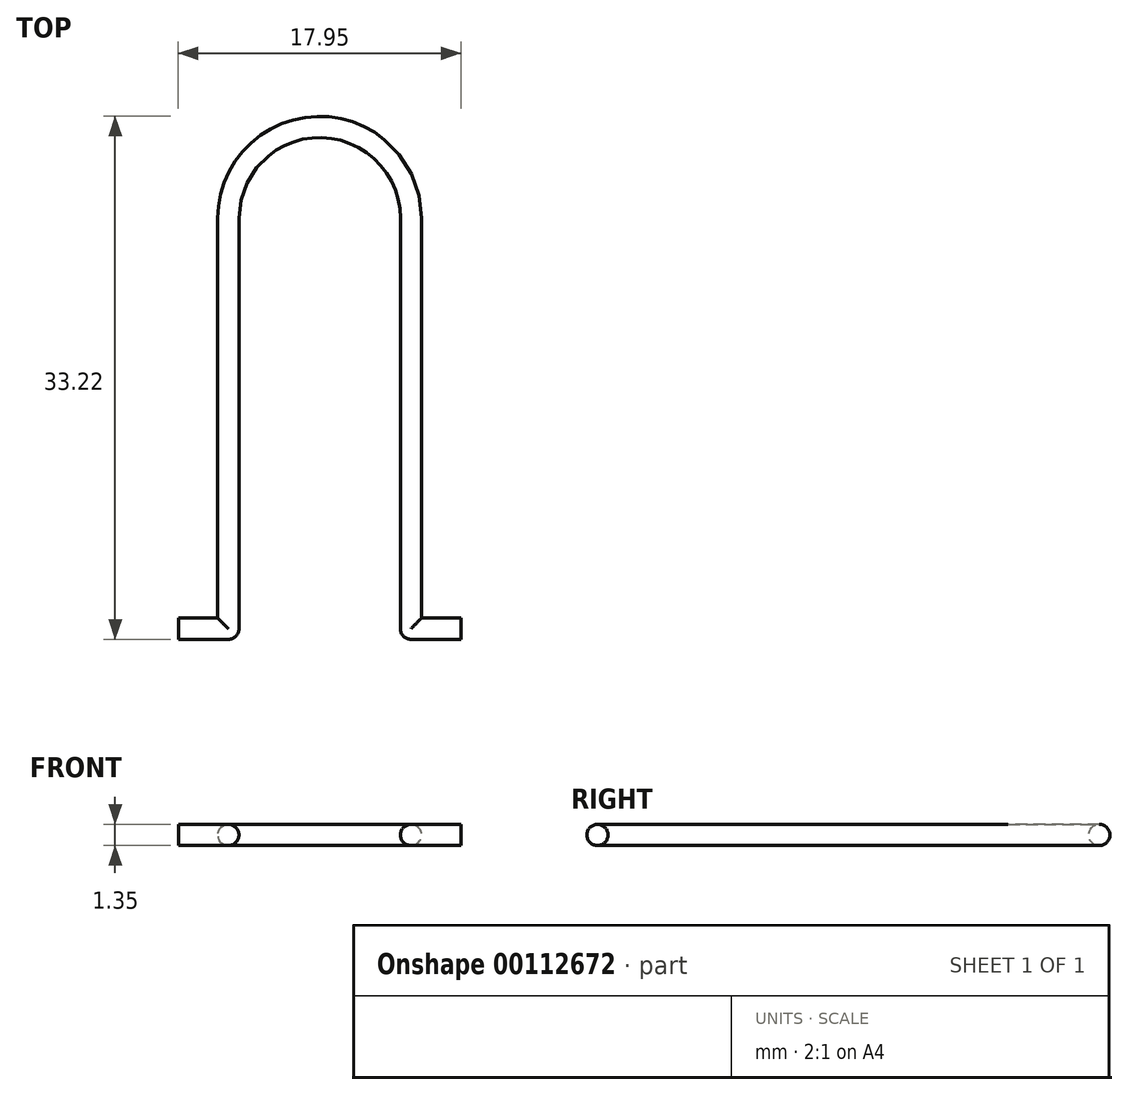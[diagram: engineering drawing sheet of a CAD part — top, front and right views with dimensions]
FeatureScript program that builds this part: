
annotation { "Feature Type Name" : "Feature", "Feature Type Description" : "" }
export const myFeature = defineFeature(function(context is Context, id is Id, definition is map)
    precondition{}
    {
        {
            var Q0;
            Q0=qCreatedBy(makeId("Top.planeOp"),FACE);
            var sketch = newSketch(context, id + "F0", { "sketchPlane" : qUnion([Q0])});
            skLineSegment(sketch, "E0.bottom", {"start": v(0, 0) * mm, "end": v(-3.85, 0) * mm});
            skLineSegment(sketch, "E0.top", {"start": v(-1.35, 1.35) * mm, "end": v(-3.85, 1.35) * mm});
            skLineSegment(sketch, "E0.right", {"start": v(-3.85, 0) * mm, "end": v(-3.85, 1.35) * mm});
            skLineSegment(sketch, "E1.left", {"start": v(-1.35, 1.35) * mm, "end": v(-1.35, 26.75) * mm});
            skLineSegment(sketch, "E1.right", {"start": v(0, 0) * mm, "end": v(0, 26.75) * mm});
            skLineSegment(sketch, "E2", {"start": v(10.26, 26.75) * mm, "end": v(10.26, 0) * mm});
            skLineSegment(sketch, "E3", {"start": v(-1.35, 26.75) * mm, "end": v(0, 26.75) * mm, "construction": true});
            skLineSegment(sketch, "E4", {"start": v(0, 26.75) * mm, "end": v(10.26, 26.75) * mm, "construction": true});
            skLineSegment(sketch, "E5", {"start": v(10.26, 26.75) * mm, "end": v(11.6, 26.75) * mm, "construction": true});
            skArc(sketch, "E6", {"start": v(11.6, 26.75) * mm, "mid": v(5.13, 33.22) * mm, "end": v(-1.35, 26.75) * mm});
            skArc(sketch, "E7", {"start": v(10.26, 26.75) * mm, "mid": v(5.13, 31.87) * mm, "end": v(0, 26.75) * mm});
            skLineSegment(sketch, "E8", {"start": v(0, 0) * mm, "end": v(10.26, 0) * mm, "construction": true});
            skLineSegment(sketch, "E9", {"start": v(10.26, 0) * mm, "end": v(14.1, 0) * mm});
            skLineSegment(sketch, "E10", {"start": v(14.1, 0) * mm, "end": v(14.1, 1.35) * mm});
            skLineSegment(sketch, "E11", {"start": v(14.1, 1.35) * mm, "end": v(11.6, 1.35) * mm});
            skLineSegment(sketch, "E12", {"start": v(11.6, 1.35) * mm, "end": v(11.6, 26.75) * mm});
            skSolve(sketch);
        }
        {
            var Q0;
            Q0 = qSketchRegion(id + "F0", true);
            extrude(context, id + "F1", {"entities" : qUnion([Q0]), "depth" : 1.35 * mm});
        }
        {
            var Q0;
            Q0=makeQuery(id+"F1.opExtrude","SWEPT_EDGE",EDGE,{"disambiguationData":[OSD([sQuery(id+"F0.wireOp",EDGE,"E0.bottom"),sQuery(id+"F0.wireOp",EDGE,"E1.right")])]});
            var Q1;
            Q1=makeQuery(id+"F1.opExtrude","CAP_EDGE",EDGE,{"disambiguationData":[OSD([sQuery(id+"F0.wireOp",EDGE,"E0.bottom")])],"isStart":false});
            var Q2;
            Q2=makeQuery(id+"F1.opExtrude","CAP_EDGE",EDGE,{"disambiguationData":[OSD([sQuery(id+"F0.wireOp",EDGE,"E0.bottom")])],"isStart":true});
            var Q3;
            Q3=makeQuery(id+"F1.opExtrude","CAP_EDGE",EDGE,{"disambiguationData":[OSD([sQuery(id+"F0.wireOp",EDGE,"E1.right")])],"isStart":false});
            var Q4;
            Q4=makeQuery(id+"F1.opExtrude","CAP_EDGE",EDGE,{"disambiguationData":[OSD([sQuery(id+"F0.wireOp",EDGE,"E1.right")])],"isStart":true});
            var Q5;
            Q5=makeQuery(id+"F1.opExtrude","CAP_EDGE",EDGE,{"disambiguationData":[OSD([sQuery(id+"F0.wireOp",EDGE,"E7")])],"isStart":false});
            var Q6;
            Q6=makeQuery(id+"F1.opExtrude","CAP_EDGE",EDGE,{"disambiguationData":[OSD([sQuery(id+"F0.wireOp",EDGE,"E7")])],"isStart":true});
            var Q7;
            Q7=makeQuery(id+"F1.opExtrude","CAP_EDGE",EDGE,{"disambiguationData":[OSD([sQuery(id+"F0.wireOp",EDGE,"E2")])],"isStart":false});
            var Q8;
            Q8=makeQuery(id+"F1.opExtrude","CAP_EDGE",EDGE,{"disambiguationData":[OSD([sQuery(id+"F0.wireOp",EDGE,"E12")])],"isStart":false});
            var Q9;
            Q9=makeQuery(id+"F1.opExtrude","CAP_EDGE",EDGE,{"disambiguationData":[OSD([sQuery(id+"F0.wireOp",EDGE,"E12")])],"isStart":true});
            var Q10;
            Q10=makeQuery(id+"F1.opExtrude","CAP_EDGE",EDGE,{"disambiguationData":[OSD([sQuery(id+"F0.wireOp",EDGE,"E6")])],"isStart":true});
            var Q11;
            Q11=makeQuery(id+"F1.opExtrude","CAP_EDGE",EDGE,{"disambiguationData":[OSD([sQuery(id+"F0.wireOp",EDGE,"E6")])],"isStart":false});
            var Q12;
            Q12=makeQuery(id+"F1.opExtrude","SWEPT_EDGE",EDGE,{"disambiguationData":[OSD([sQuery(id+"F0.wireOp",EDGE,"E2"),sQuery(id+"F0.wireOp",EDGE,"E9")])]});
            var Q13;
            Q13=makeQuery(id+"F1.opExtrude","CAP_EDGE",EDGE,{"disambiguationData":[OSD([sQuery(id+"F0.wireOp",EDGE,"E2")])],"isStart":true});
            var Q14;
            Q14=makeQuery(id+"F1.opExtrude","CAP_EDGE",EDGE,{"disambiguationData":[OSD([sQuery(id+"F0.wireOp",EDGE,"E9")])],"isStart":false});
            var Q15;
            Q15=makeQuery(id+"F1.opExtrude","CAP_EDGE",EDGE,{"disambiguationData":[OSD([sQuery(id+"F0.wireOp",EDGE,"E9")])],"isStart":true});
            var Q16;
            Q16=makeQuery(id+"F1.opExtrude","CAP_EDGE",EDGE,{"disambiguationData":[OSD([sQuery(id+"F0.wireOp",EDGE,"E11")])],"isStart":true});
            var Q17;
            Q17=makeQuery(id+"F1.opExtrude","CAP_EDGE",EDGE,{"disambiguationData":[OSD([sQuery(id+"F0.wireOp",EDGE,"E11")])],"isStart":false});
            var Q18;
            Q18=makeQuery(id+"F1.opExtrude","CAP_EDGE",EDGE,{"disambiguationData":[OSD([sQuery(id+"F0.wireOp",EDGE,"E0.top")])],"isStart":false});
            var Q19;
            Q19=makeQuery(id+"F1.opExtrude","CAP_EDGE",EDGE,{"disambiguationData":[OSD([sQuery(id+"F0.wireOp",EDGE,"E0.top")])],"isStart":true});
            fillet(context, id + "F2", {"entities" : qUnion([Q0, Q1, Q2, Q3, Q4, Q5, Q6, Q7, Q8, Q9, Q10, Q11, Q12, Q13, Q14, Q15, Q16, Q17, Q18, Q19]), "radius" : 0.67 * mm, "tangentPropagation" : true, "allowEdgeOverflow" : false});
        }
    });
